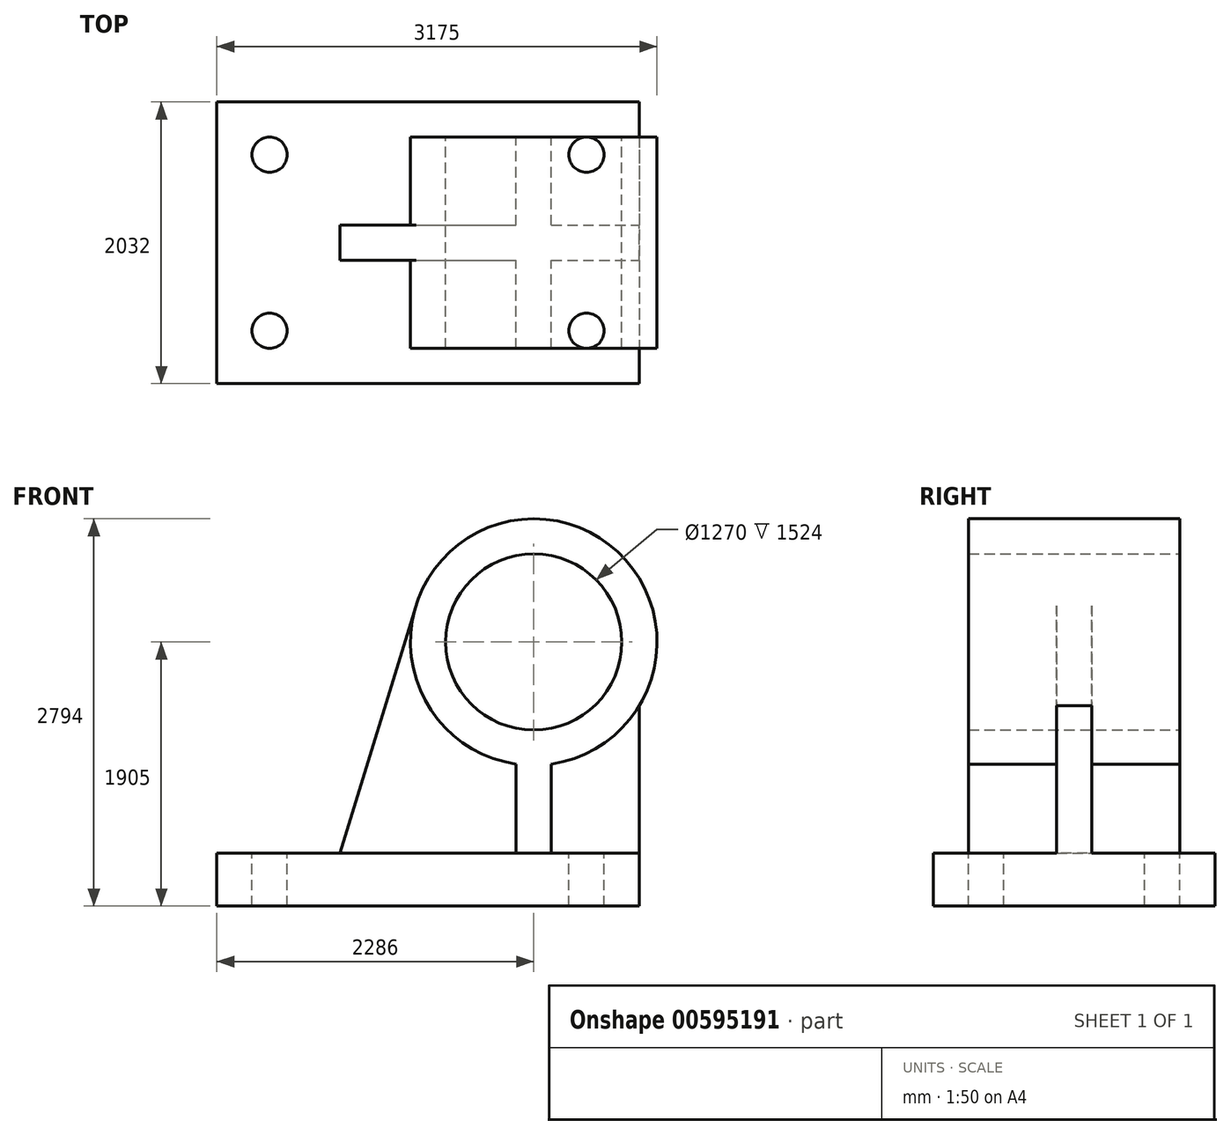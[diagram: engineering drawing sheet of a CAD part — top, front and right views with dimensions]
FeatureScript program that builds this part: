
annotation { "Feature Type Name" : "Feature", "Feature Type Description" : "" }
export const myFeature = defineFeature(function(context is Context, id is Id, definition is map)
    precondition{}
    {
        {
            var Q0;
            Q0=qCreatedBy(makeId("Top.planeOp"),FACE);
            var sketch = newSketch(context, id + "F0", { "sketchPlane" : qUnion([Q0])});
            skLineSegment(sketch, "E0.bottom", {"start": v(0, 2032) * mm, "end": v(3048, 2032) * mm});
            skLineSegment(sketch, "E0.top", {"start": v(0, 0) * mm, "end": v(3048, 0) * mm});
            skLineSegment(sketch, "E0.left", {"start": v(0, 2032) * mm, "end": v(0, 0) * mm});
            skLineSegment(sketch, "E0.right", {"start": v(3048, 2032) * mm, "end": v(3048, 0) * mm});
            skSolve(sketch);
        }
        {
            var Q0;
            Q0 = qSketchRegion(id + "F0", true);
            extrude(context, id + "F1", {"entities" : qUnion([Q0]), "depth" : 381 * mm, "offsetDistance" : 25.4 * mm});
        }
        {
            var Q0;
            Q0=makeQuery(id+"F1.opExtrude","CAP_FACE",FACE,{"disambiguationData":[OSD([sQuery(id+"F0.wireOp",EDGE,"E0.bottom"),sQuery(id+"F0.wireOp",EDGE,"E0.top"),sQuery(id+"F0.wireOp",EDGE,"E0.left"),sQuery(id+"F0.wireOp",EDGE,"E0.right")])],"isStart":false});
            var sketch = newSketch(context, id + "F2", { "sketchPlane" : qUnion([Q0])});
            skCircle(sketch, "E1", {"center": v(381, 381) * mm, "radius": 127 * mm});
            skCircle(sketch, "E2", {"center": v(2667, 1651) * mm, "radius": 127 * mm});
            skCircle(sketch, "E3", {"center": v(2667, 381) * mm, "radius": 127 * mm});
            skCircle(sketch, "E4", {"center": v(381, 1651) * mm, "radius": 127 * mm});
            skSolve(sketch);
        }
        {
            var Q0;
            Q0 = qSketchRegion(id + "F2", true);
            extrude(context, id + "F3", {"entities" : qUnion([Q0]), "operationType" : NewBodyOperationType.REMOVE, "endBound" : BoundingType.THROUGH_ALL, "oppositeDirection" : true, "depth" : 25.4 * mm, "offsetDistance" : 25.4 * mm});
        }
        {
            var Q0;
            Q0=qCreatedBy(makeId("Front.planeOp"),FACE);
            cPlane(context, id + "F4", {"entities" : qUnion([Q0]), "cplaneType" : CPlaneType.OFFSET, "offset" : 1016 * mm, "oppositeDirection" : true, "width" : 152.4 * mm, "height" : 152.4 * mm});
        }
        {
            var Q0;
            Q0=qCreatedBy(id+"F4.planeOp",FACE);
            var sketch = newSketch(context, id + "F5", { "sketchPlane" : qUnion([Q0])});
            skCircle(sketch, "E5", {"center": v(2286, 1905) * mm, "radius": 889 * mm});
            skCircle(sketch, "E6", {"center": v(2286, 1905) * mm, "radius": 635 * mm});
            skLineSegment(sketch, "E7", {"start": v(889, 381) * mm, "end": v(3048, 381) * mm});
            skLineSegment(sketch, "E8", {"start": v(3048, 381) * mm, "end": v(3048, 1905) * mm});
            skLineSegment(sketch, "E9", {"start": v(2413, 1025.12) * mm, "end": v(2413, 381) * mm});
            skLineSegment(sketch, "E10", {"start": v(2413, 381) * mm, "end": v(2159, 381) * mm});
            skLineSegment(sketch, "E11", {"start": v(2159, 381) * mm, "end": v(2159, 1025.12) * mm});
            skLineSegment(sketch, "E12", {"start": v(889, 381) * mm, "end": v(1436.04, 2165.55) * mm});
            skLineSegment(sketch, "E13", {"start": v(1436.04, 2165.55) * mm, "end": v(3048, 1905) * mm});
            skSolve(sketch);
        }
        {
            var Q0;
            {var subQ0=sQuery(id+"F5.wireOp",EDGE,"nYCBALtn-s1vB-72ol-y6tl-JgXvjZd1VQ8r");var subQ3=sQuery(id+"F5.wireOp",EDGE,"E6");var subQ4=makeQuery(id+"F5.imprint","INTERSECT",VERTEX,{"disambiguationData":[OD(0.0)],"derivedFrom":[subQ3,subQ0]});Q0=makeQuery(id+"F5.imprint","IMPRINT",FACE,{"disambiguationData":[TD([[makeQuery(id+"F5.imprint","IMPRINT",EDGE,{"disambiguationData":[TD([[subQ4,1.0]])],"derivedFrom":subQ3}),-1.0]])]});}
            var Q1;
            {var subQ0=sQuery(id+"F5.wireOp",EDGE,"fsL4YZqL-NVxp-yBPX-mmUd-zIi587aDlapN");Q1=makeQuery(id+"F5.imprint","IMPRINT",FACE,{"disambiguationData":[TD([[makeQuery(id+"F5.imprint","IMPRINT",EDGE,{"derivedFrom":subQ0}),1.0]])]});}
            var Q2;
            {var subQ0=sQuery(id+"F5.wireOp",EDGE,"fsL4YZqL-NVxp-yBPX-mmUd-zIi587aDlapN");Q2=makeQuery(id+"F5.imprint","IMPRINT",FACE,{"disambiguationData":[TD([[makeQuery(id+"F5.imprint","IMPRINT",EDGE,{"derivedFrom":subQ0}),-1.0]])]});}
            var Q3;
            {var subQ0=sQuery(id+"F5.wireOp",EDGE,"E5");var subQ1=makeQuery(id+"F5.imprint","INTERSECT",VERTEX,{"derivedFrom":[subQ0,sQuery(id+"F5.wireOp",EDGE,"E9")]});Q3=makeQuery(id+"F5.imprint","IMPRINT",FACE,{"disambiguationData":[TD([[makeQuery(id+"F5.imprint","IMPRINT",EDGE,{"disambiguationData":[TD([[subQ1,1.0]])],"derivedFrom":subQ0}),1.0]])]});}
            extrude(context, id + "F6", {"entities" : qUnion([Q0, Q1, Q2, Q3]), "depth" : 762 * mm, "offsetDistance" : 25.4 * mm, "hasSecondDirection" : true, "secondDirectionOppositeDirection" : true, "secondDirectionDepth" : 762 * mm});
        }
        {
            var Q0;
            {var subQ0=sQuery(id+"F5.wireOp",EDGE,"e9fbdrhU-6ToC-BEuk-q0fu-ijJIM0q8Zgo7");Q0=makeQuery(id+"F5.imprint","IMPRINT",FACE,{"disambiguationData":[TD([[makeQuery(id+"F5.imprint","IMPRINT",EDGE,{"derivedFrom":subQ0}),1.0]])]});}
            var Q1;
            {var subQ0=sQuery(id+"F5.wireOp",EDGE,"E9");Q1=makeQuery(id+"F5.imprint","IMPRINT",FACE,{"disambiguationData":[TD([[makeQuery(id+"F5.imprint","IMPRINT",EDGE,{"derivedFrom":subQ0}),-1.0]])]});}
            var Q2;
            {var subQ0=sQuery(id+"F5.wireOp",EDGE,"E9");Q2=makeQuery(id+"F5.imprint","IMPRINT",FACE,{"disambiguationData":[TD([[makeQuery(id+"F5.imprint","IMPRINT",EDGE,{"derivedFrom":subQ0}),1.0]])]});}
            var Q3;
            {var subQ0=sQuery(id+"F5.wireOp",EDGE,"E11");Q3=makeQuery(id+"F5.imprint","IMPRINT",FACE,{"disambiguationData":[TD([[makeQuery(id+"F5.imprint","IMPRINT",EDGE,{"derivedFrom":subQ0}),1.0]])]});}
            extrude(context, id + "F7", {"entities" : qUnion([Q0, Q1, Q2, Q3]), "depth" : 127 * mm, "offsetDistance" : 25.4 * mm, "hasSecondDirection" : true, "secondDirectionOppositeDirection" : true, "secondDirectionDepth" : 127 * mm});
        }
        {
            var Q0;
            {var subQ0=sQuery(id+"F5.wireOp",EDGE,"E9");Q0=makeQuery(id+"F5.imprint","IMPRINT",FACE,{"disambiguationData":[TD([[makeQuery(id+"F5.imprint","IMPRINT",EDGE,{"derivedFrom":subQ0}),-1.0]])]});}
            extrude(context, id + "F8", {"entities" : qUnion([Q0]), "operationType" : NewBodyOperationType.ADD, "depth" : 762 * mm, "offsetDistance" : 25.4 * mm, "hasSecondDirection" : true, "secondDirectionOppositeDirection" : true, "secondDirectionDepth" : 762 * mm});
        }
    });
